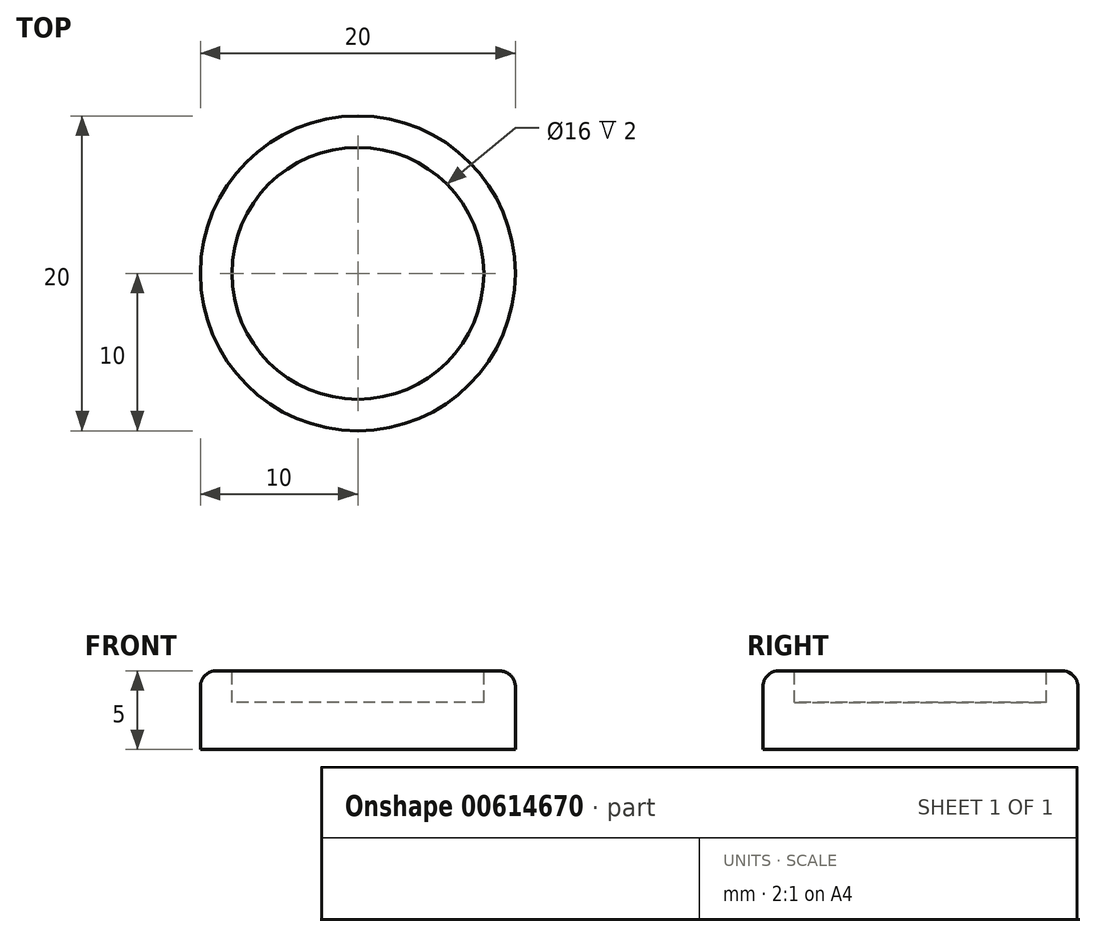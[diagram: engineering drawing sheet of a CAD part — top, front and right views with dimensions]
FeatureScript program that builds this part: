
annotation { "Feature Type Name" : "Feature", "Feature Type Description" : "" }
export const myFeature = defineFeature(function(context is Context, id is Id, definition is map)
    precondition{}
    {
        {
            var Q0;
            Q0=qCreatedBy(makeId("Top.planeOp"),FACE);
            var sketch = newSketch(context, id + "F0", { "sketchPlane" : qUnion([Q0])});
            skCircle(sketch, "E0", {"center": v(0, 0) * mm, "radius": 10 * mm});
            skSolve(sketch);
        }
        {
            var Q0;
            Q0=qSketchRegion(id+"F0",true);
            extrude(context, id + "F1", {"entities" : qUnion([Q0]), "depth" : 5 * mm, "offsetDistance" : 25 * mm});
        }
        {
            var Q0;
            Q0=makeQuery(id+"F1.opExtrude","CAP_FACE",FACE,{"disambiguationData":[OSD([sQuery(id+"F0.wireOp",EDGE,"E0")])],"isStart":false});
            var sketch = newSketch(context, id + "F2", { "sketchPlane" : qUnion([Q0])});
            skCircle(sketch, "E1", {"center": v(0, 0) * mm, "radius": 8 * mm});
            skSolve(sketch);
        }
        {
            var Q0;
            Q0=qSketchRegion(id+"F2",true);
            extrude(context, id + "F3", {"entities" : qUnion([Q0]), "operationType" : NewBodyOperationType.REMOVE, "oppositeDirection" : true, "depth" : 2 * mm, "offsetDistance" : 25 * mm});
        }
        {
            var Q0;
            Q0=makeQuery(id+"F1.opExtrude","CAP_EDGE",EDGE,{"disambiguationData":[OSD([sQuery(id+"F0.wireOp",EDGE,"E0")])],"isStart":false});
            var Q1;
            Q1=makeQuery(id+"F3.boolean.opBoolean","COPY",EDGE,{"derivedFrom":makeQuery(id+"F3.opExtrude","CAP_EDGE",EDGE,{"disambiguationData":[OSD([sQuery(id+"F2.wireOp",EDGE,"E1")])],"isStart":true})});
            fillet(context, id + "F4", {"entities" : qUnion([Q0, Q1]), "radius" : 1 * mm, "tangentPropagation" : true, "allowEdgeOverflow" : false});
        }
    });
